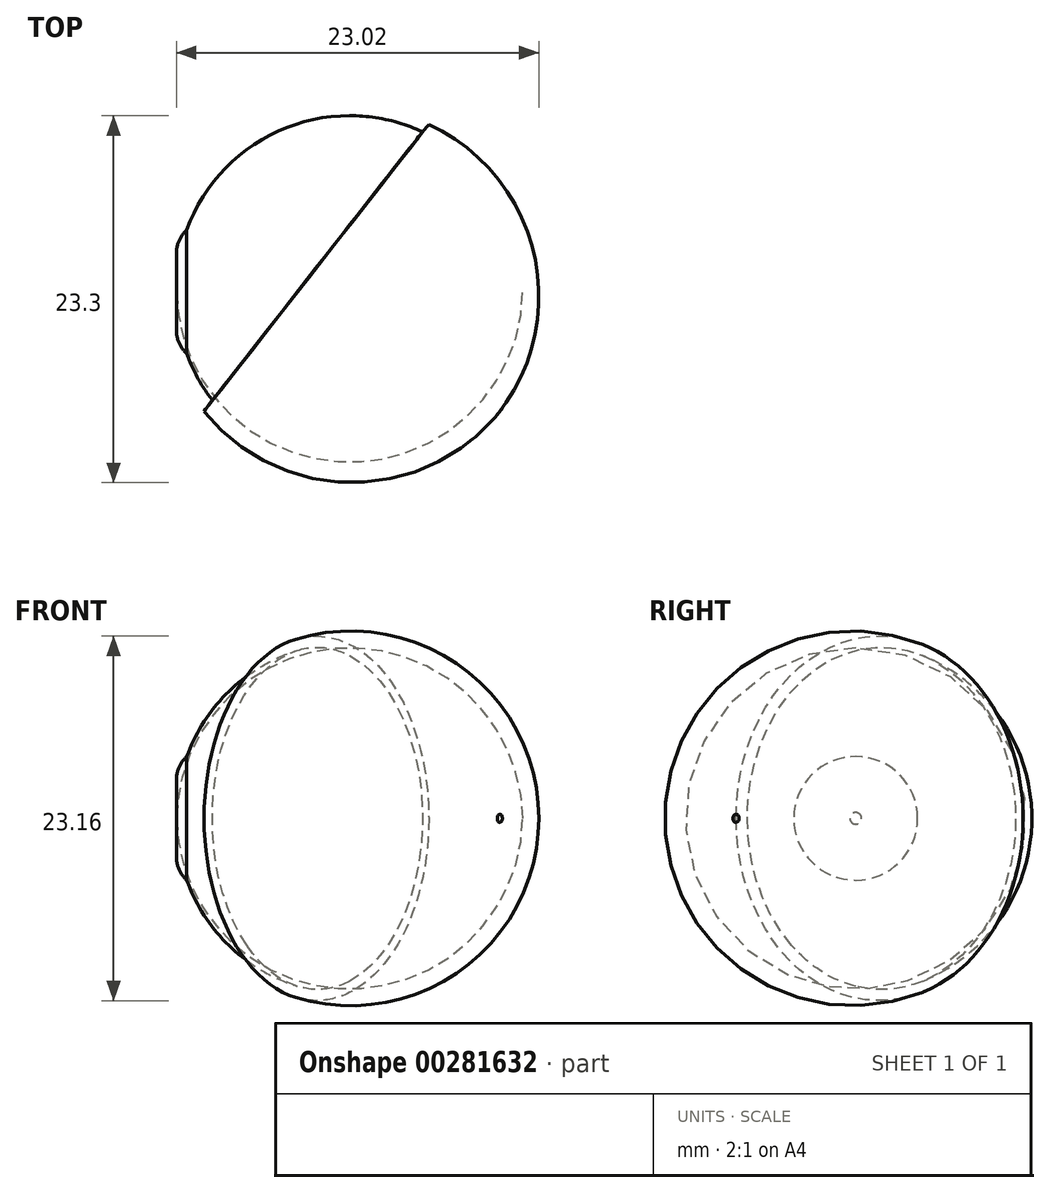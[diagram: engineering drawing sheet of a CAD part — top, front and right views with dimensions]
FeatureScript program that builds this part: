
annotation { "Feature Type Name" : "Feature", "Feature Type Description" : "" }
export const myFeature = defineFeature(function(context is Context, id is Id, definition is map)
    precondition{}
    {
        {
            var Q0;
            Q0=qCreatedBy(makeId("Top.planeOp"),FACE);
            var sketch = newSketch(context, id + "F0", { "sketchPlane" : qUnion([Q0])});
            skArc(sketch, "E0", {"start": v(22, 0) * mm, "mid": v(11, 11.18) * mm, "end": v(0, 0) * mm});
            skLineSegment(sketch, "E1", {"start": v(22, 0) * mm, "end": v(0, 0) * mm});
            skSolve(sketch);
        }
        {
            var Q0;
            Q0=makeQuery(id+"F0.imprint","IMPRINT",FACE,{"disambiguationData":[TD([[makeQuery(id+"F0.imprint","IMPRINT",EDGE,{"derivedFrom":sQuery(id+"F0.wireOp",EDGE,"E0")}),1.0]])]});
            var Q1;
            Q1=sQuery(id+"F0.wireOp",EDGE,"E1");
            revolve(context, id + "F1", {"surfaceOperationType" : NewSurfaceOperationType.NEW, "entities" : qUnion([Q0]), "axis" : qUnion([Q1]), "revolveType" : RevolveType.FULL});
        }
        {
            var Q0;
            Q0=qCreatedBy(makeId("Right.planeOp"),FACE);
            var sketch = newSketch(context, id + "F2", { "sketchPlane" : qUnion([Q0])});
            skCircle(sketch, "E2", {"center": v(0, 0) * mm, "radius": 3.93 * mm});
            skSolve(sketch);
        }
        {
            var Q0;
            Q0=makeQuery(id+"F2.imprint","IMPRINT",FACE,{"disambiguationData":[TD([[makeQuery(id+"F2.imprint","IMPRINT",EDGE,{"derivedFrom":sQuery(id+"F2.wireOp",EDGE,"E2")}),1.0]])]});
            extrude(context, id + "F3", {"entities" : qUnion([Q0]), "operationType" : NewBodyOperationType.ADD, "depth" : 3 * mm, "offsetDistance" : 25 * mm});
        }
        {
            var Q0;
            Q0=makeQuery(id+"F3.opExtrude","CAP_EDGE",EDGE,{"disambiguationData":[OSD([sQuery(id+"F2.wireOp",EDGE,"E2")])],"isStart":true});
            fillet(context, id + "F4", {"entities" : qUnion([Q0]), "radius" : 2 * mm, "tangentPropagation" : true});
        }
        {
            var Q0;
            Q0=qCreatedBy(makeId("Top.planeOp"),FACE);
            var sketch = newSketch(context, id + "F5", { "sketchPlane" : qUnion([Q0])});
            skArc(sketch, "E3", {"start": v(1.75, -7.6) * mm, "mid": v(11.15, -12.12) * mm, "end": v(20.54, -7.6) * mm});
            skLineSegment(sketch, "E4", {"start": v(1.75, -7.6) * mm, "end": v(8.53, 1.8) * mm});
            skLineSegment(sketch, "E5", {"start": v(8.53, 1.8) * mm, "end": v(20.54, -7.6) * mm});
            skPoint(sketch, "E6.orphan", {"position": v(15.3, 11.2) * mm});
            skSolve(sketch);
        }
        {
            var Q0;
            Q0=makeQuery(id+"F5.imprint","IMPRINT",FACE,{"disambiguationData":[TD([[makeQuery(id+"F5.imprint","IMPRINT",EDGE,{"derivedFrom":sQuery(id+"F5.wireOp",EDGE,"E3")}),1.0]])]});
            var Q1;
            Q1=sQuery(id+"F5.wireOp",EDGE,"E5");
            revolve(context, id + "F6", {"operationType" : NewBodyOperationType.ADD, "surfaceOperationType" : NewSurfaceOperationType.NEW, "entities" : qUnion([Q0]), "axis" : qUnion([Q1]), "revolveType" : RevolveType.FULL});
        }
        {
            var Q0;
            Q0=qCreatedBy(makeId("Right.planeOp"),FACE);
            cPlane(context, id + "F7", {"entities" : qUnion([Q0]), "cplaneType" : CPlaneType.OFFSET, "offset" : 8 * mm, "width" : 150 * mm, "height" : 150 * mm});
        }
    });
